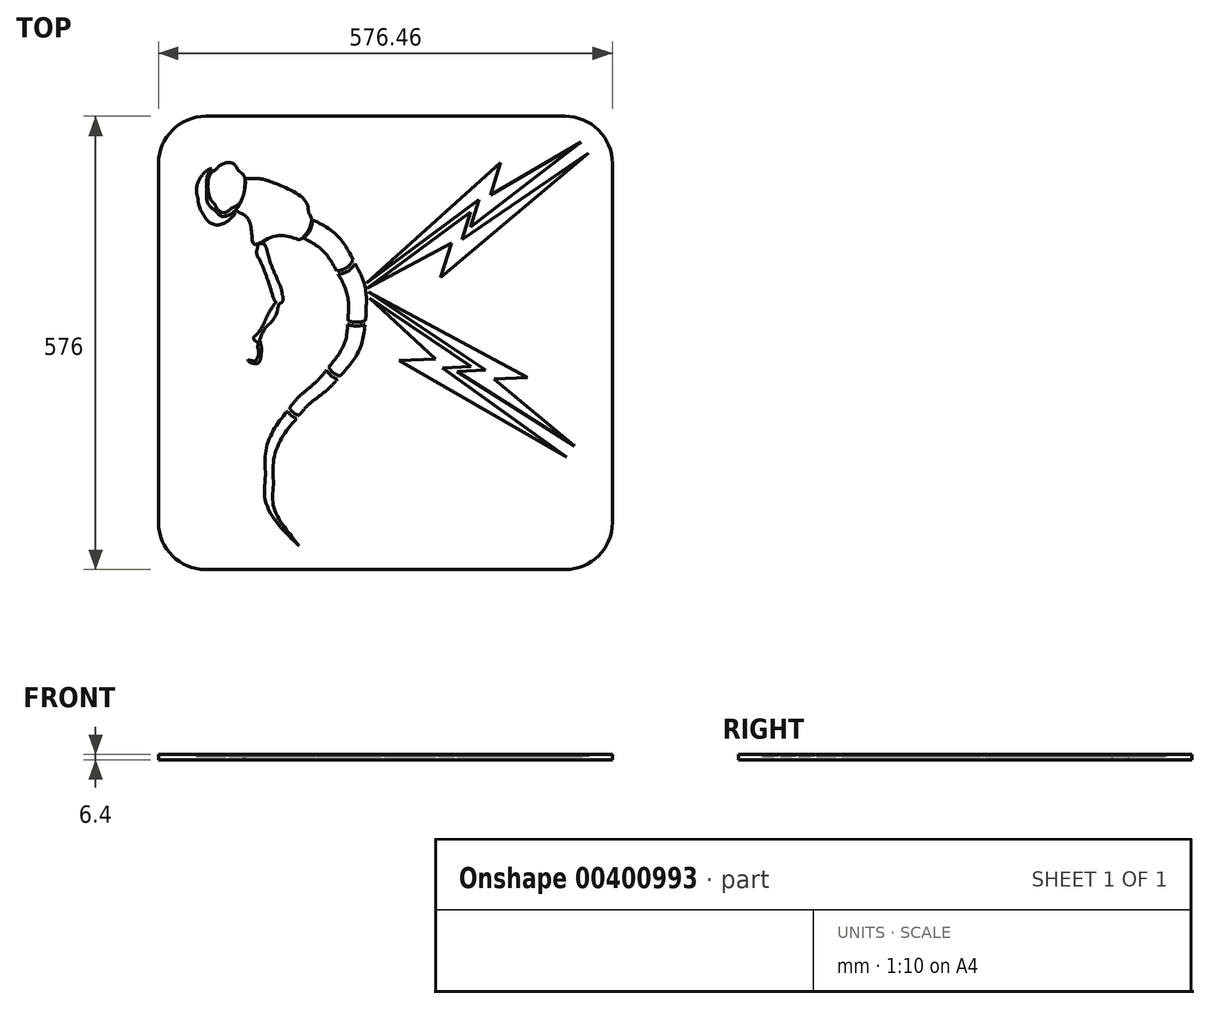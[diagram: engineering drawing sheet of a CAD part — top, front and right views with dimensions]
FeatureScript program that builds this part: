
annotation { "Feature Type Name" : "Feature", "Feature Type Description" : "" }
export const myFeature = defineFeature(function(context is Context, id is Id, definition is map)
    precondition{}
    {
        {
            var Q0;
            Q0=qCreatedBy(makeId("Top.planeOp"),FACE);
            var sketch = newSketch(context, id + "F0", { "sketchPlane" : qUnion([Q0])});
            skLineSegment(sketch, "E0", {"start": v(-288.23, 288) * mm, "end": v(288.23, 288) * mm});
            skLineSegment(sketch, "E1", {"start": v(288.23, 288) * mm, "end": v(288.23, -288) * mm});
            skLineSegment(sketch, "E2", {"start": v(288.23, -288) * mm, "end": v(-288.23, -288) * mm});
            skLineSegment(sketch, "E3", {"start": v(-288.23, -288) * mm, "end": v(-288.23, 288) * mm});
            skLineSegment(sketch, "E4", {"start": v(-21.44, 64.43) * mm, "end": v(127.04, -34.7) * mm});
            skLineSegment(sketch, "E5", {"start": v(127.04, -34.7) * mm, "end": v(90.62, -36.47) * mm});
            skLineSegment(sketch, "E6", {"start": v(90.62, -36.47) * mm, "end": v(240.34, -131) * mm});
            skLineSegment(sketch, "E7", {"start": v(240.34, -131) * mm, "end": v(137.8, -45.95) * mm});
            skLineSegment(sketch, "E8", {"start": v(137.8, -45.95) * mm, "end": v(180.61, -43.86) * mm});
            skLineSegment(sketch, "E9", {"start": v(180.61, -43.86) * mm, "end": v(-21.44, 64.43) * mm});
            skFitSpline(sketch, "E10", {"points": [v(-186.76, 218.68) * mm, v(-195, 228.5) * mm, v(-208.23, 226.72) * mm, v(-215.66, 219.95) * mm]});
            skFitSpline(sketch, "E11", {"points": [v(-215.66, 219.95) * mm, v(-223.44, 212.85) * mm, v(-224.06, 186.55) * mm, v(-218.01, 177.51) * mm]});
            skFitSpline(sketch, "E12", {"points": [v(-218.01, 177.51) * mm, v(-211.96, 168.47) * mm, v(-204.27, 165.5) * mm, v(-194.4, 172.15) * mm]});
            skFitSpline(sketch, "E13", {"points": [v(-194.4, 172.15) * mm, v(-184.54, 178.79) * mm, v(-178.52, 208.84) * mm, v(-186.76, 218.68) * mm]});
            skLineSegment(sketch, "E14", {"start": v(-24.2, 76.02) * mm, "end": v(119.12, 181.86) * mm});
            skLineSegment(sketch, "E15", {"start": v(119.12, 181.86) * mm, "end": v(108.33, 147.03) * mm});
            skLineSegment(sketch, "E16", {"start": v(108.33, 147.03) * mm, "end": v(248.38, 255.4) * mm});
            skLineSegment(sketch, "E17", {"start": v(248.38, 255.4) * mm, "end": v(133.38, 188.12) * mm});
            skLineSegment(sketch, "E18", {"start": v(133.38, 188.12) * mm, "end": v(146.06, 229.07) * mm});
            skLineSegment(sketch, "E19", {"start": v(146.06, 229.07) * mm, "end": v(-24.2, 76.02) * mm});
            skFitSpline(sketch, "E20", {"points": [v(-231.04, 215.19) * mm, v(-237.22, 206.32) * mm, v(-239.99, 193.1) * mm, v(-238.18, 183.37) * mm]});
            skFitSpline(sketch, "E21", {"points": [v(-238.18, 183.37) * mm, v(-236.11, 172.28) * mm, v(-223.6, 153.17) * mm, v(-218.15, 151.01) * mm]});
            skFitSpline(sketch, "E22", {"points": [v(-218.15, 151.01) * mm, v(-214.92, 149.74) * mm, v(-202.44, 153.38) * mm, v(-197.8, 157.34) * mm]});
            skFitSpline(sketch, "E23", {"points": [v(-197.8, 157.34) * mm, v(-195.44, 159.35) * mm, v(-192, 162.97) * mm, v(-192.43, 168.01) * mm]});
            skFitSpline(sketch, "E24", {"points": [v(-192.43, 168.01) * mm, v(-193.74, 165.61) * mm, v(-207.2, 160.77) * mm, v(-214.69, 166.84) * mm]});
            skFitSpline(sketch, "E25", {"points": [v(-214.69, 166.84) * mm, v(-222.09, 172.85) * mm, v(-226.4, 179.1) * mm, v(-226.91, 194.66) * mm]});
            skFitSpline(sketch, "E26", {"points": [v(-226.91, 194.66) * mm, v(-227.22, 203.94) * mm, v(-226.12, 212.22) * mm, v(-220.8, 221.71) * mm]});
            skLineSegment(sketch, "E27", {"start": v(-20.55, 56.81) * mm, "end": v(108.68, -29.69) * mm});
            skLineSegment(sketch, "E28", {"start": v(108.68, -29.69) * mm, "end": v(72.38, -31.62) * mm});
            skLineSegment(sketch, "E29", {"start": v(72.38, -31.62) * mm, "end": v(230.03, -144.68) * mm});
            skLineSegment(sketch, "E30", {"start": v(230.03, -144.68) * mm, "end": v(17.31, -22.33) * mm});
            skLineSegment(sketch, "E31", {"start": v(17.31, -22.33) * mm, "end": v(63.27, -20.2) * mm});
            skLineSegment(sketch, "E32", {"start": v(63.27, -20.2) * mm, "end": v(-20.55, 56.81) * mm});
            skFitSpline(sketch, "E33", {"points": [v(-125.07, -86.9) * mm, v(-141.63, -109.83) * mm, v(-152.1, -137.76) * mm, v(-152.12, -167.93) * mm]});
            skFitSpline(sketch, "E34", {"points": [v(-152.12, -167.93) * mm, v(-152.12, -201.88) * mm, v(-133.77, -233.35) * mm, v(-110.08, -257.68) * mm]});
            skFitSpline(sketch, "E35", {"points": [v(-110.08, -257.68) * mm, v(-127.49, -234.97) * mm, v(-142.03, -208.3) * mm, v(-142.06, -179.7) * mm]});
            skFitSpline(sketch, "E36", {"points": [v(-142.06, -179.7) * mm, v(-142.06, -148.75) * mm, v(-131.22, -119.78) * mm, v(-112.92, -96.04) * mm]});
            skFitSpline(sketch, "E37", {"points": [v(-112.92, -96.04) * mm, v(-117.54, -93.83) * mm, v(-121.67, -90.72) * mm, v(-125.07, -86.9) * mm]});
            skLineSegment(sketch, "E38", {"start": v(-22.73, 69.78) * mm, "end": v(108.13, 166.32) * mm});
            skLineSegment(sketch, "E39", {"start": v(108.13, 166.32) * mm, "end": v(97.54, 131.55) * mm});
            skLineSegment(sketch, "E40", {"start": v(97.54, 131.55) * mm, "end": v(257.7, 241.02) * mm});
            skLineSegment(sketch, "E41", {"start": v(257.7, 241.02) * mm, "end": v(69.97, 82.98) * mm});
            skLineSegment(sketch, "E42", {"start": v(69.97, 82.98) * mm, "end": v(83.7, 126.9) * mm});
            skLineSegment(sketch, "E43", {"start": v(83.7, 126.9) * mm, "end": v(-22.73, 69.78) * mm});
            skFitSpline(sketch, "E44", {"points": [v(-75.12, -34.64) * mm, v(-82.44, -43.54) * mm, v(-90.88, -51.91) * mm, v(-100.06, -59.76) * mm]});
            skFitSpline(sketch, "E45", {"points": [v(-100.06, -59.76) * mm, v(-108.1, -66.63) * mm, v(-115.53, -74.42) * mm, v(-122.12, -82.95) * mm]});
            skFitSpline(sketch, "E46", {"points": [v(-122.12, -82.95) * mm, v(-118.8, -86.94) * mm, v(-114.6, -90.1) * mm, v(-109.85, -92.2) * mm]});
            skFitSpline(sketch, "E47", {"points": [v(-109.85, -92.2) * mm, v(-102.66, -83.48) * mm, v(-94.45, -75.52) * mm, v(-85.38, -68.52) * mm]});
            skFitSpline(sketch, "E48", {"points": [v(-85.38, -68.52) * mm, v(-76.65, -61.78) * mm, v(-68.46, -54.25) * mm, v(-61.1, -46.04) * mm]});
            skFitSpline(sketch, "E49", {"points": [v(-61.1, -46.04) * mm, v(-66.6, -43.4) * mm, v(-71.42, -39.5) * mm, v(-75.12, -34.64) * mm]});
            skFitSpline(sketch, "E50", {"points": [v(-186.78, 173.05) * mm, v(-190.2, 168.51) * mm, v(-177.38, 160.95) * mm, v(-169.61, 136.17) * mm]});
            skFitSpline(sketch, "E51", {"points": [v(-169.61, 136.17) * mm, v(-166.2, 125.29) * mm, v(-142.31, 135.27) * mm, v(-113.49, 132.55) * mm]});
            skFitSpline(sketch, "E52", {"points": [v(-113.49, 132.55) * mm, v(-107.4, 131.97) * mm, v(-94.02, 153.7) * mm, v(-97.46, 165.1) * mm]});
            skFitSpline(sketch, "E53", {"points": [v(-97.46, 165.1) * mm, v(-102.3, 181.1) * mm, v(-128.14, 197.86) * mm, v(-149.3, 206.2) * mm]});
            skFitSpline(sketch, "E54", {"points": [v(-92.45, 156.1) * mm, v(-94.14, 147.45) * mm, v(-98.17, 139.44) * mm, v(-104.1, 132.93) * mm]});
            skFitSpline(sketch, "E55", {"points": [v(-104.1, 132.93) * mm, v(-86.47, 122.94) * mm, v(-72.22, 108.57) * mm, v(-62.4, 91.63) * mm]});
            skFitSpline(sketch, "E56", {"points": [v(-62.4, 91.63) * mm, v(-53.83, 93.29) * mm, v(-46.24, 98.22) * mm, v(-41.24, 105.39) * mm]});
            skFitSpline(sketch, "E57", {"points": [v(-41.24, 105.39) * mm, v(-53, 126.4) * mm, v(-70.56, 144.13) * mm, v(-92.45, 156.1) * mm]});
            skFitSpline(sketch, "E58", {"points": [v(-38.71, 100.68) * mm, v(-44.1, 93.93) * mm, v(-51.59, 89.19) * mm, v(-60, 87.21) * mm]});
            skFitSpline(sketch, "E59", {"points": [v(-60, 87.21) * mm, v(-51.82, 71.52) * mm, v(-47.32, 53.86) * mm, v(-47.3, 35.54) * mm]});
            skFitSpline(sketch, "E60", {"points": [v(-47.3, 35.54) * mm, v(-47.31, 33.16) * mm, v(-47.4, 30.8) * mm, v(-47.58, 28.48) * mm]});
            skFitSpline(sketch, "E61", {"points": [v(-47.58, 28.48) * mm, v(-44.05, 27.24) * mm, v(-40.33, 26.6) * mm, v(-36.6, 26.59) * mm]});
            skFitSpline(sketch, "E62", {"points": [v(-36.6, 26.59) * mm, v(-32.79, 26.6) * mm, v(-29.02, 27.26) * mm, v(-25.43, 28.54) * mm]});
            skFitSpline(sketch, "E63", {"points": [v(-25.43, 28.54) * mm, v(-24.91, 32.93) * mm, v(-24.63, 37.39) * mm, v(-24.62, 41.9) * mm]});
            skFitSpline(sketch, "E64", {"points": [v(-24.62, 41.9) * mm, v(-24.65, 62.7) * mm, v(-29.63, 82.77) * mm, v(-38.71, 100.68) * mm]});
            skFitSpline(sketch, "E65", {"points": [v(-48.1, 23.57) * mm, v(-50.65, 3.7) * mm, v(-59.4, -14.39) * mm, v(-72.02, -30.74) * mm]});
            skFitSpline(sketch, "E66", {"points": [v(-72.02, -30.74) * mm, v(-68.42, -35.82) * mm, v(-63.49, -39.8) * mm, v(-57.76, -42.22) * mm]});
            skFitSpline(sketch, "E67", {"points": [v(-57.76, -42.22) * mm, v(-41.81, -23.36) * mm, v(-30.21, -1.15) * mm, v(-26.19, 23.24) * mm]});
            skFitSpline(sketch, "E68", {"points": [v(-26.19, 23.24) * mm, v(-29.57, 22.28) * mm, v(-33.07, 21.78) * mm, v(-36.59, 21.77) * mm]});
            skFitSpline(sketch, "E69", {"points": [v(-36.59, 21.77) * mm, v(-40.5, 21.78) * mm, v(-44.37, 22.4) * mm, v(-48.1, 23.57) * mm]});
            skFitSpline(sketch, "E70", {"points": [v(-158.31, 126.15) * mm, v(-160.21, 126.16) * mm, v(-161.89, 124.05) * mm, v(-162.87, 119) * mm]});
            skFitSpline(sketch, "E71", {"points": [v(-162.87, 119) * mm, v(-163.81, 114.2) * mm, v(-157.85, 101.86) * mm, v(-154.13, 92.06) * mm]});
            skFitSpline(sketch, "E72", {"points": [v(-154.13, 92.06) * mm, v(-149.84, 80.75) * mm, v(-146.3, 69.88) * mm, v(-142.66, 58.55) * mm]});
            skFitSpline(sketch, "E73", {"points": [v(-142.66, 58.55) * mm, v(-141.58, 55.2) * mm, v(-140.29, 53) * mm, v(-138.96, 51.7) * mm]});
            skFitSpline(sketch, "E74", {"points": [v(-138.96, 51.7) * mm, v(-139.74, 50.96) * mm, v(-140.59, 49.92) * mm, v(-141.47, 48.56) * mm]});
            skFitSpline(sketch, "E75", {"points": [v(-141.47, 48.56) * mm, v(-148.93, 36.99) * mm, v(-157.76, 18.32) * mm, v(-165.29, 9.22) * mm]});
            skFitSpline(sketch, "E76", {"points": [v(-165.29, 9.22) * mm, v(-167.47, 6.58) * mm, v(-166.04, 2.9) * mm, v(-163.81, 2.01) * mm]});
            skFitSpline(sketch, "E77", {"points": [v(-163.81, 2.01) * mm, v(-161.86, -1.01) * mm, v(-162.25, -4.53) * mm, v(-161.76, -8) * mm]});
            skFitSpline(sketch, "E78", {"points": [v(-161.76, -8) * mm, v(-160.99, -11.68) * mm, v(-161.7, -16.27) * mm, v(-163.42, -19.97) * mm]});
            skFitSpline(sketch, "E79", {"points": [v(-163.42, -19.97) * mm, v(-164.36, -21.98) * mm, v(-164.25, -23) * mm, v(-169.73, -22.56) * mm]});
            skFitSpline(sketch, "E80", {"points": [v(-169.73, -22.56) * mm, v(-170.78, -22.48) * mm, v(-172.85, -21.87) * mm, v(-174.78, -21.2) * mm]});
            skFitSpline(sketch, "E81", {"points": [v(-174.78, -21.2) * mm, v(-174.14, -22.35) * mm, v(-173.2, -24.2) * mm, v(-172.06, -24.6) * mm]});
            skFitSpline(sketch, "E82", {"points": [v(-172.06, -24.6) * mm, v(-168.97, -25.7) * mm, v(-163.13, -26.14) * mm, v(-160.37, -24.36) * mm]});
            skFitSpline(sketch, "E83", {"points": [v(-160.37, -24.36) * mm, v(-159.1, -21.62) * mm, v(-158.42, -18.45) * mm, v(-158.14, -15.52) * mm]});
            skFitSpline(sketch, "E84", {"points": [v(-158.14, -15.52) * mm, v(-157.53, -10.69) * mm, v(-157.63, -5.8) * mm, v(-158.56, -1.03) * mm]});
            skFitSpline(sketch, "E85", {"points": [v(-158.56, -1.03) * mm, v(-158.85, 0.47) * mm, v(-159.1, 1.42) * mm, v(-160.02, 3.34) * mm]});
            skFitSpline(sketch, "E86", {"points": [v(-160.02, 3.34) * mm, v(-160.04, 3.38) * mm, v(-160.07, 3.41) * mm, v(-160.1, 3.46) * mm]});
            skFitSpline(sketch, "E87", {"points": [v(-160.1, 3.46) * mm, v(-159.8, 3.85) * mm, v(-159.5, 4.32) * mm, v(-159.24, 4.88) * mm]});
            skFitSpline(sketch, "E88", {"points": [v(-159.24, 4.88) * mm, v(-152.66, 18.69) * mm, v(-141.66, 30.86) * mm, v(-136.39, 45.65) * mm]});
            skFitSpline(sketch, "E89", {"points": [v(-136.39, 45.65) * mm, v(-135.7, 47.6) * mm, v(-135.35, 49.14) * mm, v(-135.27, 50.32) * mm]});
            skFitSpline(sketch, "E90", {"points": [v(-135.27, 50.32) * mm, v(-132.26, 50.93) * mm, v(-130.03, 55.77) * mm, v(-131.17, 61.5) * mm]});
            skFitSpline(sketch, "E91", {"points": [v(-131.17, 61.5) * mm, v(-132.8, 69.76) * mm, v(-135.74, 76.86) * mm, v(-138.67, 83.7) * mm]});
            skFitSpline(sketch, "E92", {"points": [v(-138.67, 83.7) * mm, v(-142.58, 92.88) * mm, v(-146.53, 102.71) * mm, v(-149.07, 111.88) * mm]});
            skFitSpline(sketch, "E93", {"points": [v(-149.07, 111.88) * mm, v(-151.36, 120.15) * mm, v(-155.15, 126.12) * mm, v(-158.31, 126.15) * mm]});
            skFitSpline(sketch, "E94", {"points": [v(-220.8, 221.71) * mm, v(-226.81, 219.26) * mm, v(-231.04, 215.19) * mm], "startDerivative": vector(-13.29, -2.94) * mm, "endDerivative": vector(-7.87, -11.33) * mm});
            skFitSpline(sketch, "E95", {"points": [v(-178.23, 208.51) * mm, v(-159.78, 208.51) * mm, v(-149.3, 206.2) * mm], "startDerivative": vector(40.78, 2.62) * mm, "endDerivative": vector(24.82, -8.6) * mm});
            skFitSpline(sketch, "E96", {"points": [v(-178.23, 208.51) * mm, v(-179.7, 191.2) * mm, v(-186.78, 173.05) * mm], "startDerivative": vector(-1.63, -38) * mm, "endDerivative": vector(-21.17, -37.99) * mm});
            skSolve(sketch);
        }
        {
            var Q0;
            Q0=makeQuery(id+"F0.imprint","IMPRINT",FACE,{"disambiguationData":[TD([[makeQuery(id+"F0.imprint","IMPRINT",EDGE,{"derivedFrom":sQuery(id+"F0.wireOp",EDGE,"E0")}),-1.0]])]});
            extrude(context, id + "F1", {"entities" : qUnion([Q0]), "depth" : 6.4 * mm});
        }
        {
            var Q0;
            Q0=makeQuery(id+"F0.imprint","IMPRINT",FACE,{"disambiguationData":[TD([[makeQuery(id+"F0.imprint","IMPRINT",EDGE,{"derivedFrom":sQuery(id+"F0.wireOp",EDGE,"E20")}),1.0]])]});
            var Q1;
            Q1=makeQuery(id+"F0.imprint","IMPRINT",FACE,{"disambiguationData":[TD([[makeQuery(id+"F0.imprint","IMPRINT",EDGE,{"derivedFrom":sQuery(id+"F0.wireOp",EDGE,"E10")}),1.0]])]});
            var Q2;
            Q2=makeQuery(id+"F0.imprint","IMPRINT",FACE,{"disambiguationData":[TD([[makeQuery(id+"F0.imprint","IMPRINT",EDGE,{"derivedFrom":sQuery(id+"F0.wireOp",EDGE,"E50")}),1.0]])]});
            var Q3;
            Q3=makeQuery(id+"F0.imprint","IMPRINT",FACE,{"disambiguationData":[TD([[makeQuery(id+"F0.imprint","IMPRINT",EDGE,{"derivedFrom":sQuery(id+"F0.wireOp",EDGE,"E70")}),1.0]])]});
            var Q4;
            Q4=makeQuery(id+"F0.imprint","IMPRINT",FACE,{"disambiguationData":[TD([[makeQuery(id+"F0.imprint","IMPRINT",EDGE,{"derivedFrom":sQuery(id+"F0.wireOp",EDGE,"E54")}),1.0]])]});
            var Q5;
            Q5=makeQuery(id+"F0.imprint","IMPRINT",FACE,{"disambiguationData":[TD([[makeQuery(id+"F0.imprint","IMPRINT",EDGE,{"derivedFrom":sQuery(id+"F0.wireOp",EDGE,"E58")}),1.0]])]});
            var Q6;
            Q6=makeQuery(id+"F0.imprint","IMPRINT",FACE,{"disambiguationData":[TD([[makeQuery(id+"F0.imprint","IMPRINT",EDGE,{"derivedFrom":sQuery(id+"F0.wireOp",EDGE,"E38")}),-1.0]])]});
            var Q7;
            Q7=makeQuery(id+"F0.imprint","IMPRINT",FACE,{"disambiguationData":[TD([[makeQuery(id+"F0.imprint","IMPRINT",EDGE,{"derivedFrom":sQuery(id+"F0.wireOp",EDGE,"E14")}),1.0]])]});
            var Q8;
            Q8=makeQuery(id+"F0.imprint","IMPRINT",FACE,{"disambiguationData":[TD([[makeQuery(id+"F0.imprint","IMPRINT",EDGE,{"derivedFrom":sQuery(id+"F0.wireOp",EDGE,"E27")}),-1.0]])]});
            var Q9;
            Q9=makeQuery(id+"F0.imprint","IMPRINT",FACE,{"disambiguationData":[TD([[makeQuery(id+"F0.imprint","IMPRINT",EDGE,{"derivedFrom":sQuery(id+"F0.wireOp",EDGE,"E4")}),1.0]])]});
            var Q10;
            Q10=makeQuery(id+"F0.imprint","IMPRINT",FACE,{"disambiguationData":[TD([[makeQuery(id+"F0.imprint","IMPRINT",EDGE,{"derivedFrom":sQuery(id+"F0.wireOp",EDGE,"E65")}),1.0]])]});
            var Q11;
            Q11=makeQuery(id+"F0.imprint","IMPRINT",FACE,{"disambiguationData":[TD([[makeQuery(id+"F0.imprint","IMPRINT",EDGE,{"derivedFrom":sQuery(id+"F0.wireOp",EDGE,"E44")}),1.0]])]});
            var Q12;
            Q12=makeQuery(id+"F0.imprint","IMPRINT",FACE,{"disambiguationData":[TD([[makeQuery(id+"F0.imprint","IMPRINT",EDGE,{"derivedFrom":sQuery(id+"F0.wireOp",EDGE,"E33")}),1.0]])]});
            extrude(context, id + "F2", {"entities" : qUnion([Q0, Q1, Q2, Q3, Q4, Q5, Q6, Q7, Q8, Q9, Q10, Q11, Q12]), "operationType" : NewBodyOperationType.ADD, "depth" : 4 * mm});
        }
        {
            var Q0;
            Q0=makeQuery(id+"F1.opExtrude","SWEPT_EDGE",EDGE,{"disambiguationData":[OSD([sQuery(id+"F0.wireOp",EDGE,"E2"),sQuery(id+"F0.wireOp",EDGE,"E3")])]});
            var Q1;
            Q1=makeQuery(id+"F1.opExtrude","SWEPT_EDGE",EDGE,{"disambiguationData":[OSD([sQuery(id+"F0.wireOp",EDGE,"E0"),sQuery(id+"F0.wireOp",EDGE,"E3")])]});
            var Q2;
            Q2=makeQuery(id+"F1.opExtrude","SWEPT_EDGE",EDGE,{"disambiguationData":[OSD([sQuery(id+"F0.wireOp",EDGE,"E1"),sQuery(id+"F0.wireOp",EDGE,"E2")])]});
            var Q3;
            Q3=makeQuery(id+"F1.opExtrude","SWEPT_EDGE",EDGE,{"disambiguationData":[OSD([sQuery(id+"F0.wireOp",EDGE,"E0"),sQuery(id+"F0.wireOp",EDGE,"E1")])]});
            fillet(context, id + "F3", {"entities" : qUnion([Q0, Q1, Q2, Q3]), "radius" : 60 * mm, "tangentPropagation" : true, "allowEdgeOverflow" : false});
        }
    });
